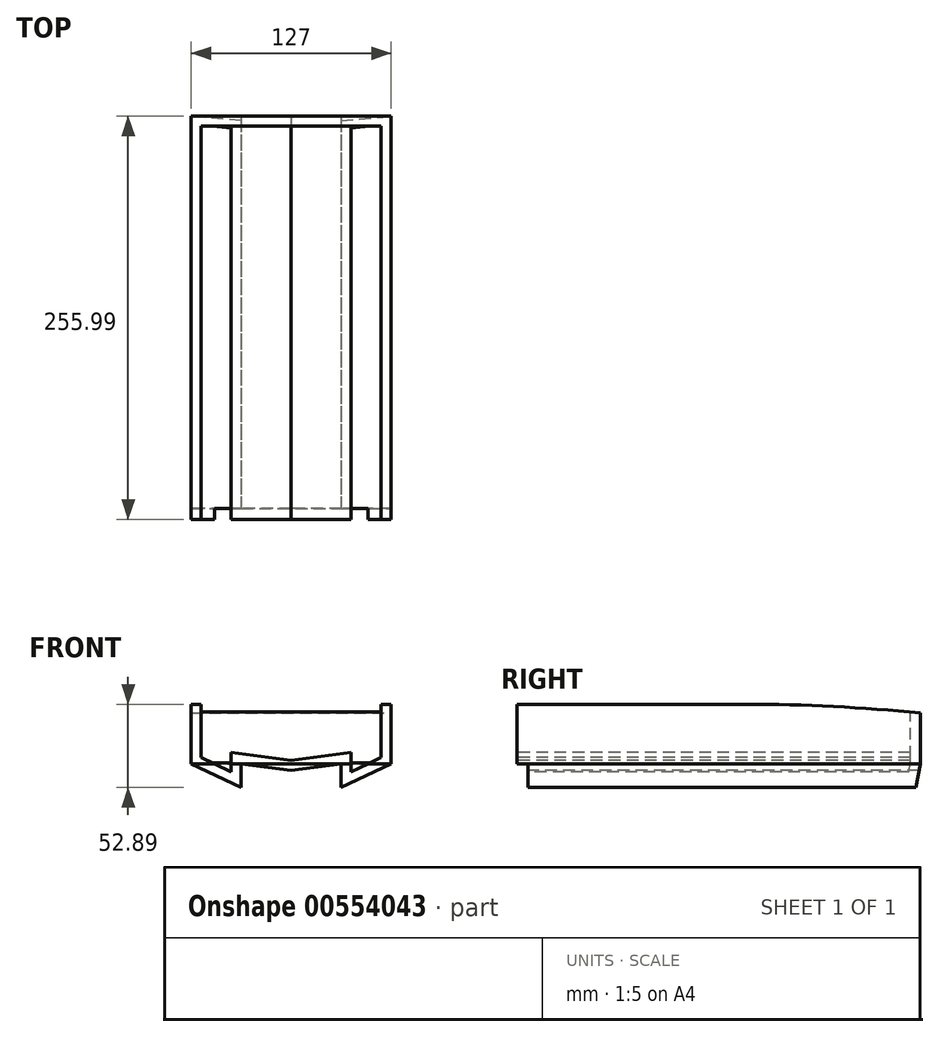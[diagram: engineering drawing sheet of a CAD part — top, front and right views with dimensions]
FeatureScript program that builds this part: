
annotation { "Feature Type Name" : "Feature", "Feature Type Description" : "" }
export const myFeature = defineFeature(function(context is Context, id is Id, definition is map)
    precondition{}
    {
        {
            var Q0;
            Q0=qCreatedBy(makeId("Right.planeOp"),FACE);
            var sketch = newSketch(context, id + "F0", { "sketchPlane" : qUnion([Q0])});
            skLineSegment(sketch, "E0", {"start": v(0, 15.07) * mm, "end": v(254, 15.07) * mm});
            skLineSegment(sketch, "E1", {"start": v(254, 15.07) * mm, "end": v(-254, 15.07) * mm});
            skLineSegment(sketch, "E2", {"start": v(254, 15.07) * mm, "end": v(245.2, -34.96) * mm});
            skLineSegment(sketch, "E3", {"start": v(231.07, 15.07) * mm, "end": v(231.07, -61.13) * mm, "construction": true});
            skLineSegment(sketch, "E4", {"start": v(245.2, -34.96) * mm, "end": v(-49.93, -34.96) * mm});
            skArc(sketch, "E5", {"start": v(-254, 15.07) * mm, "mid": v(-154.98, -22.27) * mm, "end": v(-49.93, -34.96) * mm});
            skSolve(sketch);
        }
        {
            var Q0;
            Q0 = qSketchRegion(id + "F0", true);
            extrude(context, id + "F1", {"entities" : qUnion([Q0]), "depth" : 127 * mm, "offsetDistance" : 25.4 * mm});
        }
        {
            var Q0;
            Q0=makeQuery(id+"F1.opExtrude","SWEPT_FACE",FACE,{"disambiguationData":[OSD([sQuery(id+"F0.wireOp",EDGE,"E2")])]});
            var sketch = newSketch(context, id + "F2", { "sketchPlane" : qUnion([Q0])});
            skLineSegment(sketch, "E6", {"start": v(-127, 8.02) * mm, "end": v(0, 8.02) * mm});
            skLineSegment(sketch, "E7", {"start": v(0, 8.02) * mm, "end": v(-63.5, 8.02) * mm});
            skLineSegment(sketch, "E8", {"start": v(-63.5, 8.02) * mm, "end": v(-31.75, 8.02) * mm});
            skLineSegment(sketch, "E9", {"start": v(-31.75, 8.02) * mm, "end": v(-31.75, -7.22) * mm});
            skLineSegment(sketch, "E10", {"start": v(-31.75, -7.22) * mm, "end": v(0, 8.02) * mm});
            skLineSegment(sketch, "E11", {"start": v(-63.5, 8.02) * mm, "end": v(-63.5, -27.89) * mm, "construction": true});
            skLineSegment(sketch, "E12.MirrorCS", {"start": v(-95.25, 8.02) * mm, "end": v(-95.25, -7.22) * mm});
            skLineSegment(sketch, "E13.MirrorCS", {"start": v(-95.25, -7.22) * mm, "end": v(-127, 8.02) * mm});
            skSolve(sketch);
        }
        {
            var Q0;
            {var subQ2=sQuery(id+"F2.wireOp",EDGE,"E12.MirrorCS");Q0=makeQuery(id+"F2.imprint","IMPRINT",FACE,{"disambiguationData":[TD([[makeQuery(id+"F2.imprint","IMPRINT",EDGE,{"derivedFrom":subQ2}),-1.0]])]});}
            var Q1;
            {var subQ2=sQuery(id+"F2.wireOp",EDGE,"E9");Q1=makeQuery(id+"F2.imprint","IMPRINT",FACE,{"disambiguationData":[TD([[makeQuery(id+"F2.imprint","IMPRINT",EDGE,{"derivedFrom":subQ2}),1.0]])]});}
            var Q2;
            Q2=makeQuery(id+"F1.opExtrude","CAP_EDGE",EDGE,{"disambiguationData":[OSD([sQuery(id+"F0.wireOp",EDGE,"E4")])],"isStart":false});
            var Q3;
            Q3=makeQuery(id+"F1.opExtrude","CAP_EDGE",EDGE,{"disambiguationData":[OSD([sQuery(id+"F0.wireOp",EDGE,"E5")])],"isStart":false});
            sweep(context, id + "F3", {"operationType" : NewBodyOperationType.ADD, "profiles" : qUnion([Q0, Q1]), "path" : qUnion([Q2, Q3])});
        }
        {
            var Q0;
            {var subQ0=sQuery(id+"F2.wireOp",EDGE,"E6");var subQ1=sQuery(id+"F0.wireOp",EDGE,"E4");var subQ2=sQuery(id+"F0.wireOp",EDGE,"E2");Q0=makeQuery(id+"F3.boolean.opBoolean","MERGE",FACE,{"derivedFrom":[makeQuery(id+"F1.opExtrude","SWEPT_FACE",FACE,{"disambiguationData":[OSD([subQ2])]}),makeQuery(id+"F3.opSweep","CAP_FACE",FACE,{"disambiguationData":[OSD([subQ2,subQ1,subQ0,sQuery(id+"F2.wireOp",EDGE,"E12.MirrorCS"),sQuery(id+"F2.wireOp",EDGE,"E13.MirrorCS")])],"isStart":true}),makeQuery(id+"F3.opSweep","CAP_FACE",FACE,{"disambiguationData":[OSD([subQ2,subQ1,subQ0,sQuery(id+"F2.wireOp",EDGE,"E9"),sQuery(id+"F2.wireOp",EDGE,"E10")])],"isStart":true})]});}
            var sketch = newSketch(context, id + "F4", { "sketchPlane" : qUnion([Q0])});
            skLineSegment(sketch, "E14", {"start": v(-95.25, 8.02) * mm, "end": v(-63.5, 3.87) * mm});
            skPoint(sketch, "E14.endSnap0", {"position": v(-63.5, 8.02) * mm});
            skLineSegment(sketch, "E15", {"start": v(-63.5, 3.87) * mm, "end": v(-31.75, 8.02) * mm});
            skSolve(sketch);
        }
        {
            var Q0;
            Q0=makeQuery(id+"F4.imprint","IMPRINT",FACE,{"disambiguationData":[TD([[makeQuery(id+"F4.imprint","IMPRINT",EDGE,{"derivedFrom":sQuery(id+"F4.wireOp",EDGE,"E14")}),1.0]])]});
            var Q1;
            {var subQ0=sQuery(id+"F0.wireOp",EDGE,"E4");Q1=makeQuery(id+"F3.boolean.opBoolean","MERGE",EDGE,{"derivedFrom":[makeQuery(id+"F1.opExtrude","CAP_EDGE",EDGE,{"disambiguationData":[OSD([subQ0])],"isStart":false}),makeQuery(id+"F3.opSweep","SWEPT_EDGE",EDGE,{"disambiguationData":[OSD([sQuery(id+"F0.wireOp",EDGE,"E2"),subQ0,sQuery(id+"F2.wireOp",EDGE,"E6"),sQuery(id+"F2.wireOp",EDGE,"E13.MirrorCS")])]})]});}
            var Q2;
            {var subQ0=sQuery(id+"F0.wireOp",EDGE,"E5");Q2=makeQuery(id+"F3.boolean.opBoolean","MERGE",EDGE,{"derivedFrom":[makeQuery(id+"F1.opExtrude","CAP_EDGE",EDGE,{"disambiguationData":[OSD([subQ0])],"isStart":false}),makeQuery(id+"F3.opSweep","SWEPT_EDGE",EDGE,{"disambiguationData":[OSD([sQuery(id+"F0.wireOp",EDGE,"E2"),subQ0,sQuery(id+"F2.wireOp",EDGE,"E6"),sQuery(id+"F2.wireOp",EDGE,"E13.MirrorCS")])]})]});}
            sweep(context, id + "F5", {"operationType" : NewBodyOperationType.ADD, "profiles" : qUnion([Q0]), "path" : qUnion([Q1, Q2])});
        }
        {
            var Q0;
            Q0=makeQuery(id+"F1.opExtrude","SWEPT_FACE",FACE,{"disambiguationData":[OSD([sQuery(id+"F0.wireOp",EDGE,"E0"),sQuery(id+"F0.wireOp",EDGE,"E1")])]});
            var sketch = newSketch(context, id + "F6", { "sketchPlane" : qUnion([Q0])});
            skArc(sketch, "E16", {"start": v(0, -156.46) * mm, "mid": v(10.5, -211.39) * mm, "end": v(31.75, -263.12) * mm});
            skLineSegment(sketch, "E17", {"start": v(0, -156.46) * mm, "end": v(-86.43, -199.53) * mm});
            skLineSegment(sketch, "E18", {"start": v(-86.43, -199.53) * mm, "end": v(5.86, -312.85) * mm});
            skLineSegment(sketch, "E19", {"start": v(5.86, -312.85) * mm, "end": v(31.75, -263.12) * mm});
            skLineSegment(sketch, "E20", {"start": v(63.5, -254) * mm, "end": v(63.5, -186.2) * mm, "construction": true});
            skArc(sketch, "E21.MirrorCS", {"start": v(127, -156.46) * mm, "mid": v(116.5, -211.39) * mm, "end": v(95.25, -263.12) * mm});
            skLineSegment(sketch, "E22.MirrorCS", {"start": v(121.14, -312.85) * mm, "end": v(95.25, -263.12) * mm});
            skLineSegment(sketch, "E23.MirrorCS", {"start": v(213.43, -199.53) * mm, "end": v(121.14, -312.85) * mm});
            skLineSegment(sketch, "E24.MirrorCS", {"start": v(127, -156.46) * mm, "end": v(213.43, -199.53) * mm});
            skSolve(sketch);
        }
        {
            var Q0;
            Q0 = qSketchRegion(id + "F6", true);
            extrude(context, id + "F7", {"entities" : qUnion([Q0]), "operationType" : NewBodyOperationType.REMOVE, "oppositeDirection" : true, "depth" : 71.63 * mm, "offsetDistance" : 25.4 * mm});
        }
        {
            var Q0;
            Q0=makeQuery(id+"F1.opExtrude","CAP_FACE",FACE,{"disambiguationData":[OSD([sQuery(id+"F0.wireOp",EDGE,"E0"),sQuery(id+"F0.wireOp",EDGE,"E1"),sQuery(id+"F0.wireOp",EDGE,"E2"),sQuery(id+"F0.wireOp",EDGE,"E4"),sQuery(id+"F0.wireOp",EDGE,"E5")])],"isStart":false});
            var sketch = newSketch(context, id + "F8", { "sketchPlane" : qUnion([Q0])});
            skLineSegment(sketch, "E25", {"start": v(-260.62, 4.22) * mm, "end": v(252.1, 4.22) * mm});
            skLineSegment(sketch, "E26", {"start": v(252.1, 4.22) * mm, "end": v(-269.42, 4.22) * mm});
            skLineSegment(sketch, "E27", {"start": v(-269.42, 4.22) * mm, "end": v(-258.05, 32.11) * mm});
            skLineSegment(sketch, "E28", {"start": v(-258.05, 32.11) * mm, "end": v(259.4, 32.11) * mm});
            skLineSegment(sketch, "E29", {"start": v(259.4, 32.11) * mm, "end": v(252.1, 4.22) * mm});
            skSolve(sketch);
        }
        {
            var Q0;
            Q0 = qSketchRegion(id + "F8", true);
            extrude(context, id + "F9", {"entities" : qUnion([Q0]), "operationType" : NewBodyOperationType.REMOVE, "oppositeDirection" : true, "depth" : 179.07 * mm, "offsetDistance" : 25.4 * mm});
        }
        {
            var Q0;
            Q0=makeQuery(id+"F1.opExtrude","CAP_FACE",FACE,{"disambiguationData":[OSD([sQuery(id+"F0.wireOp",EDGE,"E0"),sQuery(id+"F0.wireOp",EDGE,"E1"),sQuery(id+"F0.wireOp",EDGE,"E2"),sQuery(id+"F0.wireOp",EDGE,"E4"),sQuery(id+"F0.wireOp",EDGE,"E5")])],"isStart":false});
            var sketch = newSketch(context, id + "F10", { "sketchPlane" : qUnion([Q0])});
            skLineSegment(sketch, "E30", {"start": v(-265.84, 2.92) * mm, "end": v(134.9, 2.92) * mm});
            skLineSegment(sketch, "E31", {"start": v(252.1, 4.22) * mm, "end": v(245.2, -34.96) * mm});
            skLineSegment(sketch, "E32", {"start": v(245.2, -34.96) * mm, "end": v(245.2, 4.22) * mm});
            skLineSegment(sketch, "E33", {"start": v(245.2, -34.96) * mm, "end": v(245.2, -3.21) * mm, "construction": true});
            skArc(sketch, "E34", {"start": v(250.79, -3.21) * mm, "mid": v(192.92, 1.39) * mm, "end": v(134.9, 2.92) * mm});
            skLineSegment(sketch, "E35", {"start": v(250.79, -3.21) * mm, "end": v(257.45, 34.72) * mm});
            skLineSegment(sketch, "E36", {"start": v(257.45, 34.72) * mm, "end": v(-303.16, 34.72) * mm});
            skLineSegment(sketch, "E37", {"start": v(-303.16, 34.72) * mm, "end": v(-265.84, 2.92) * mm});
            skSolve(sketch);
        }
        {
            var Q0;
            Q0 = qSketchRegion(id + "F10", true);
            extrude(context, id + "F11", {"entities" : qUnion([Q0]), "operationType" : NewBodyOperationType.REMOVE, "oppositeDirection" : true, "depth" : 157.73 * mm, "offsetDistance" : 25.4 * mm});
        }
        {
            var Q0;
            Q0=makeQuery(id+"F11.boolean.opBoolean","COPY",FACE,{"derivedFrom":makeQuery(id+"F11.opExtrude","SWEPT_FACE",FACE,{"disambiguationData":[OSD([sQuery(id+"F10.wireOp",EDGE,"E34")])]})});
            var Q1;
            Q1=makeQuery(id+"F11.boolean.opBoolean","COPY",FACE,{"derivedFrom":makeQuery(id+"F11.opExtrude","SWEPT_FACE",FACE,{"disambiguationData":[OSD([sQuery(id+"F10.wireOp",EDGE,"E30")])]})});
            shell(context, id + "F12", {"entities" : qUnion([Q0, Q1]), "thickness" : 6.35 * mm});
        }
        {
            var Q0;
            Q0=makeQuery(id+"F1.opExtrude","CAP_FACE",FACE,{"disambiguationData":[OSD([sQuery(id+"F0.wireOp",EDGE,"E0"),sQuery(id+"F0.wireOp",EDGE,"E1"),sQuery(id+"F0.wireOp",EDGE,"E2"),sQuery(id+"F0.wireOp",EDGE,"E4"),sQuery(id+"F0.wireOp",EDGE,"E5")])],"isStart":false});
            var sketch = newSketch(context, id + "F13", { "sketchPlane" : qUnion([Q0])});
            skLineSegment(sketch, "E38", {"start": v(245.2, -18.8) * mm, "end": v(-10.78, -18.8) * mm, "construction": true});
            skPoint(sketch, "E38.endSnap0", {"position": v(-10.78, 2.92) * mm});
            skLineSegment(sketch, "E39", {"start": v(-10.78, -18.8) * mm, "end": v(-10.78, 2.92) * mm});
            skLineSegment(sketch, "E40", {"start": v(-10.78, -18.8) * mm, "end": v(-10.78, -34.96) * mm});
            skLineSegment(sketch, "E41.MirrorCS", {"start": v(-266.77, -18.8) * mm, "end": v(-10.78, -18.8) * mm, "construction": true});
            skLineSegment(sketch, "E42", {"start": v(-266.77, -18.8) * mm, "end": v(-3.8, -18.8) * mm, "construction": true});
            skLineSegment(sketch, "E43", {"start": v(-3.8, -18.8) * mm, "end": v(-3.8, -57.71) * mm, "construction": true});
            skLineSegment(sketch, "E44", {"start": v(-3.8, -18.8) * mm, "end": v(-3.8, -57.71) * mm});
            skLineSegment(sketch, "E45", {"start": v(-3.8, -38.26) * mm, "end": v(-3.8, -18.8) * mm});
            skLineSegment(sketch, "E46", {"start": v(-3.8, -34.96) * mm, "end": v(-3.8, -57.71) * mm});
            skLineSegment(sketch, "E47", {"start": v(-3.8, -34.96) * mm, "end": v(-10.78, -34.96) * mm});
            skLineSegment(sketch, "E48", {"start": v(-10.78, -34.96) * mm, "end": v(-10.78, 6.82) * mm});
            skLineSegment(sketch, "E49", {"start": v(-10.78, 6.82) * mm, "end": v(-286.57, 12.3) * mm});
            skLineSegment(sketch, "E50", {"start": v(-286.57, 12.3) * mm, "end": v(-295.06, -75.68) * mm});
            skLineSegment(sketch, "E51", {"start": v(-295.06, -75.68) * mm, "end": v(-3.8, -57.71) * mm});
            skSolve(sketch);
        }
        {
            var Q0;
            Q0 = qSketchRegion(id + "F13", true);
            extrude(context, id + "F14", {"entities" : qUnion([Q0]), "operationType" : NewBodyOperationType.REMOVE, "oppositeDirection" : true, "depth" : 181.86 * mm, "offsetDistance" : 25.4 * mm});
        }
    });
